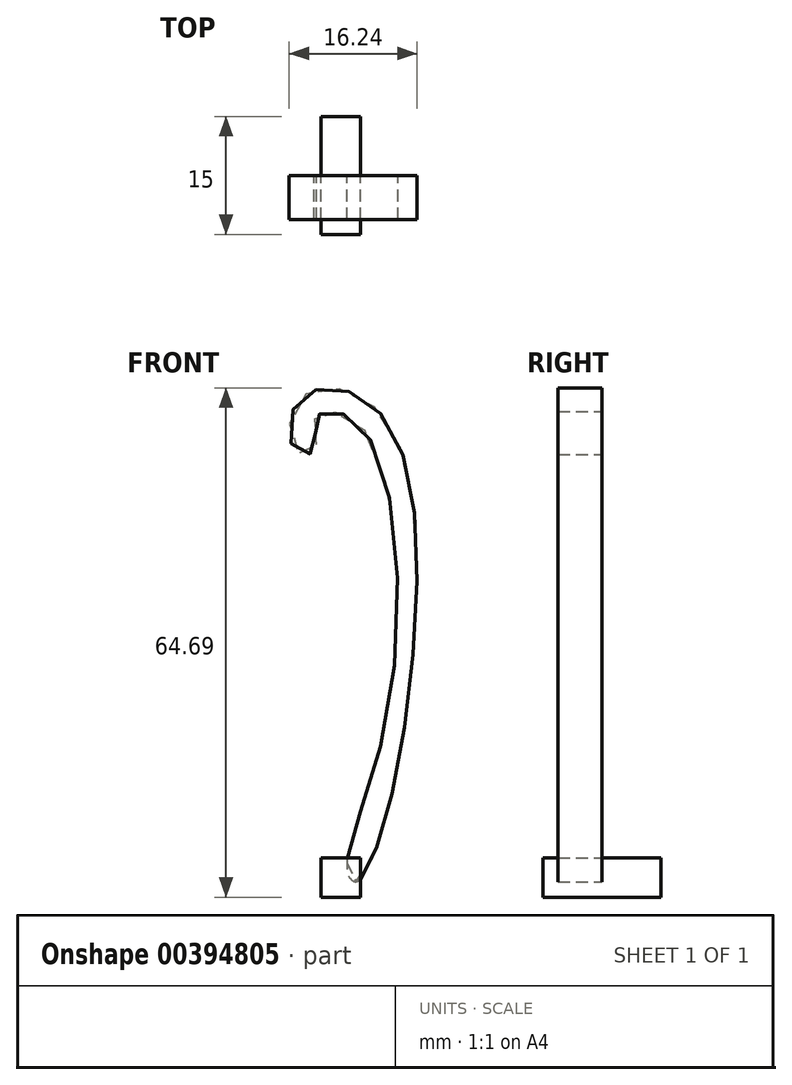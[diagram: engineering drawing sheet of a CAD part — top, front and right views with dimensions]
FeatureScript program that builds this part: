
annotation { "Feature Type Name" : "Feature", "Feature Type Description" : "" }
export const myFeature = defineFeature(function(context is Context, id is Id, definition is map)
    precondition{}
    {
        {
            var Q0;
            Q0=qCreatedBy(makeId("Front.planeOp"),FACE);
            var sketch = newSketch(context, id + "F0", { "sketchPlane" : qUnion([Q0])});
            skLineSegment(sketch, "E0.0", {"start": v(-2.5, 2.5) * mm, "end": v(2.5, 2.5) * mm});
            skLineSegment(sketch, "E0.1", {"start": v(2.5, 2.5) * mm, "end": v(2.5, -2.5) * mm});
            skLineSegment(sketch, "E0.2", {"start": v(2.5, -2.5) * mm, "end": v(-2.5, -2.5) * mm});
            skLineSegment(sketch, "E0.3", {"start": v(-2.5, -2.5) * mm, "end": v(-2.5, 2.5) * mm});
            skPoint(sketch, "E0.0.midPoint", {"position": v(0, 2.5) * mm});
            skSolve(sketch);
        }
        {
            var Q0;
            Q0 = qSketchRegion(id + "F0", true);
            extrude(context, id + "F1", {"entities" : qUnion([Q0]), "endBound" : BoundingType.SYMMETRIC, "depth" : 15 * mm});
        }
        {
            var Q0;
            Q0=qCreatedBy(makeId("Front.planeOp"),FACE);
            var sketch = newSketch(context, id + "F2", { "sketchPlane" : qUnion([Q0])});
            skLineSegment(sketch, "E1", {"start": v(10.96, 0) * mm, "end": v(10.96, 60) * mm, "construction": true});
            skFitSpline(sketch, "E2", {"points": [v(1.9, -0.54) * mm, v(5.33, 6.1) * mm, v(9.6, 34.9) * mm, v(6.28, 57.3) * mm, v(-0.87, 62.16) * mm, v(-5.84, 59.88) * mm, v(-5.64, 54.08) * mm, v(-3.25, 54.39) * mm, v(-3.36, 58.02) * mm, v(-1.7, 59.16) * mm, v(3.38, 56.25) * mm, v(6.07, 21.43) * mm, v(0.79, 1.12) * mm, v(1.9, -0.54) * mm]});
            skSolve(sketch);
        }
        {
            var Q0;
            Q0 = qSketchRegion(id + "F2", true);
            extrude(context, id + "F3", {"entities" : qUnion([Q0]), "depth" : 5.6 * mm});
        }
    });
